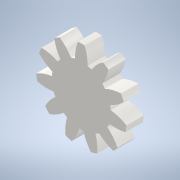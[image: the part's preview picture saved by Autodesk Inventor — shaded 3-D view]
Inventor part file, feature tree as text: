
AUTODESK INVENTOR PART (.ipt)
format: ipt  version: 2022 (Build 260153000, 153)  size: 190,976 bytes
history: native  units: mm (DEFAULTED — no unit token found)
features: plane x3, other x3, sketch x2, extrude x1
ambient origin geometry x8: Origin, YZ Plane, XZ Plane, XY Plane, X Axis, Y Axis, Z Axis, Center Point
bodies: Solid1 (feature_tree)
feature tree (9):
  extrude  "Extrusion1"  Depth=5.0mm TaperAngle=0.0deg
  plane  "Work Plane2"
  plane  "Work Plane8"
  plane  "Work Plane9"
  other  "Spur Gear"
  sketch  "Sketch1"  dims[d0=26.0mm d1=5.0mm d2=0.0mm]
  sketch  "Sketch2"  dims[d3=22.0mm d4=10.0mm d5=0.0mm d16=22.0mm d17=0.0mm d34=2.855993mm d39=0.0mm d41=0.0mm d43=22.0mm d46=22.0mm d47=0.0mm d48=0.0mm]
  other  "Srf1"
  other  "Pitch Diameter"
